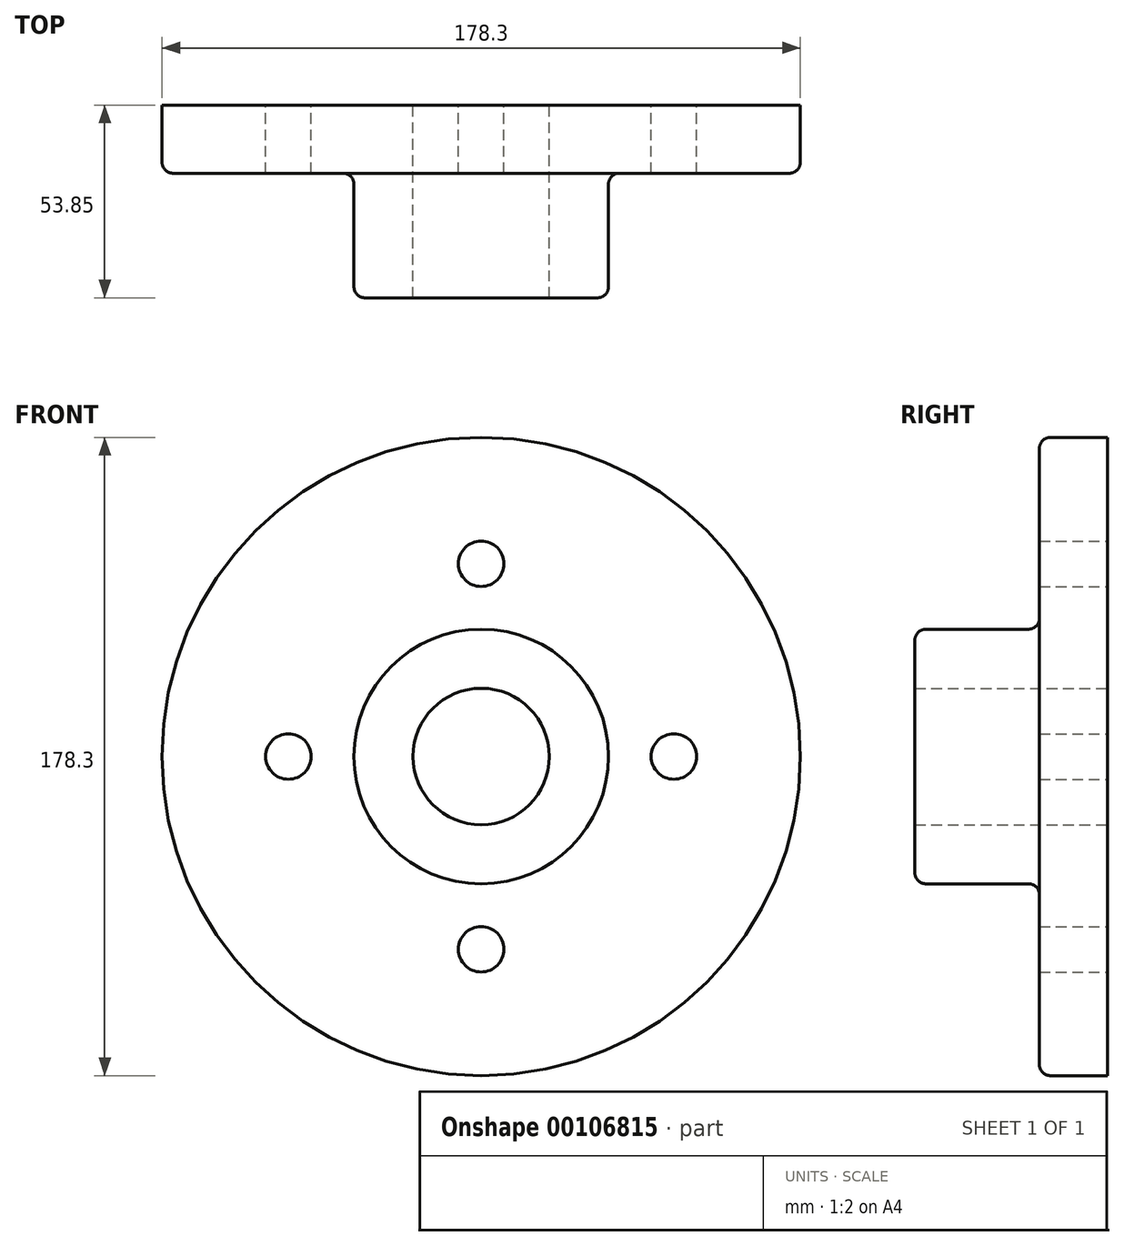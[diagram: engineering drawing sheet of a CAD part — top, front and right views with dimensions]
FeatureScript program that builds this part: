
annotation { "Feature Type Name" : "Feature", "Feature Type Description" : "" }
export const myFeature = defineFeature(function(context is Context, id is Id, definition is map)
    precondition{}
    {
        {
            var Q0;
            Q0=qCreatedBy(makeId("Right.planeOp"),FACE);
            var sketch = newSketch(context, id + "F0", { "sketchPlane" : qUnion([Q0])});
            skLineSegment(sketch, "E0", {"start": v(100.19, 0) * mm, "end": v(-100.65, 0) * mm});
            skLineSegment(sketch, "E1", {"start": v(0, 19.05) * mm, "end": v(0, 89.15) * mm});
            skLineSegment(sketch, "E2", {"start": v(0, 89.15) * mm, "end": v(-19.05, 89.15) * mm});
            skLineSegment(sketch, "E3", {"start": v(-19.05, 89.15) * mm, "end": v(-19.05, 35.55) * mm});
            skLineSegment(sketch, "E4", {"start": v(-19.05, 35.55) * mm, "end": v(-53.85, 35.55) * mm});
            skLineSegment(sketch, "E5", {"start": v(-53.85, 35.55) * mm, "end": v(-53.85, 19.05) * mm});
            skLineSegment(sketch, "E6", {"start": v(-53.85, 19.05) * mm, "end": v(0, 19.05) * mm});
            skSolve(sketch);
        }
        {
            var Q0;
            Q0=makeQuery(id+"F0.imprint","IMPRINT",FACE,{"disambiguationData":[TD([[makeQuery(id+"F0.imprint","IMPRINT",EDGE,{"derivedFrom":sQuery(id+"F0.wireOp",EDGE,"E1")}),1.0]])]});
            var Q1;
            Q1=sQuery(id+"F0.wireOp",EDGE,"E0");
            revolve(context, id + "F1", {"entities" : qUnion([Q0]), "axis" : qUnion([Q1]), "revolveType" : RevolveType.FULL});
        }
        {
            var Q0;
            Q0=makeQuery(id+"F1.opRevolve","SWEPT_EDGE",EDGE,{"disambiguationData":[OSD([sQuery(id+"F0.wireOp",EDGE,"E2"),sQuery(id+"F0.wireOp",EDGE,"E3")])]});
            var Q1;
            Q1=makeQuery(id+"F1.opRevolve","SWEPT_EDGE",EDGE,{"disambiguationData":[OSD([sQuery(id+"F0.wireOp",EDGE,"E3"),sQuery(id+"F0.wireOp",EDGE,"E4")])]});
            var Q2;
            Q2=makeQuery(id+"F1.opRevolve","SWEPT_EDGE",EDGE,{"disambiguationData":[OSD([sQuery(id+"F0.wireOp",EDGE,"E4"),sQuery(id+"F0.wireOp",EDGE,"E5")])]});
            fillet(context, id + "F2", {"entities" : qUnion([Q0, Q1, Q2]), "radius" : 3.05 * mm, "tangentPropagation" : true, "allowEdgeOverflow" : false});
        }
        {
            var Q0;
            Q0=qCreatedBy(makeId("Front.planeOp"),FACE);
            var sketch = newSketch(context, id + "F3", { "sketchPlane" : qUnion([Q0])});
            skCircle(sketch, "E7", {"center": v(0, 0) * mm, "radius": 53.85 * mm, "construction": true});
            skCircle(sketch, "E8", {"center": v(0, 53.85) * mm, "radius": 6.35 * mm});
            skCircle(sketch, "E9", {"center": v(53.85, 0) * mm, "radius": 6.35 * mm});
            skCircle(sketch, "E10", {"center": v(-53.85, 0) * mm, "radius": 6.35 * mm});
            skCircle(sketch, "E11", {"center": v(0, -53.85) * mm, "radius": 6.35 * mm});
            skLineSegment(sketch, "E12", {"start": v(-68.03, 0) * mm, "end": v(77.46, 0) * mm, "construction": true});
            skLineSegment(sketch, "E13", {"start": v(0, 53.85) * mm, "end": v(0, -64.08) * mm, "construction": true});
            skSolve(sketch);
        }
        {
            var Q0;
            Q0 = qSketchRegion(id + "F3", true);
            var Q1;
            Q1=sQuery(id+"F3.wireOp",EDGE,"E8");
            extrude(context, id + "F4", {"entities" : qUnion([Q0]), "operationType" : NewBodyOperationType.REMOVE, "surfaceEntities" : qUnion([Q1]), "endBound" : BoundingType.THROUGH_ALL, "depth" : 25.4 * mm});
        }
    });
